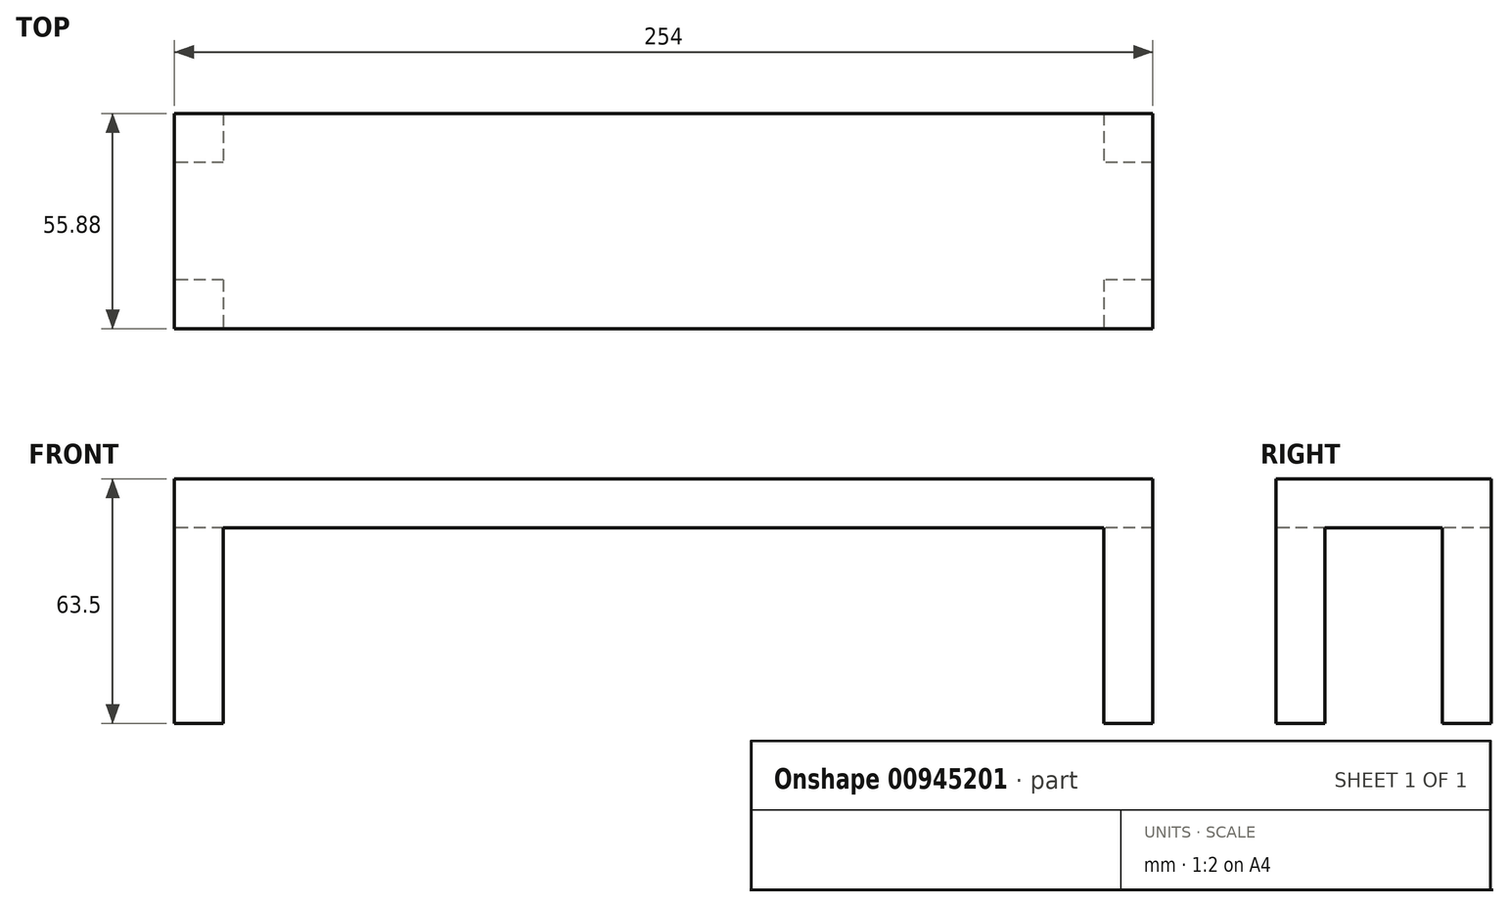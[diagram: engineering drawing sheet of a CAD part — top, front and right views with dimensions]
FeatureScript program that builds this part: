
annotation { "Feature Type Name" : "Feature", "Feature Type Description" : "" }
export const myFeature = defineFeature(function(context is Context, id is Id, definition is map)
    precondition{}
    {
        {
            var Q0;
            Q0=qCreatedBy(makeId("Top.planeOp"),FACE);
            var sketch = newSketch(context, id + "F0", { "sketchPlane" : qUnion([Q0])});
            skLineSegment(sketch, "E0.bottom", {"start": v(-235.66, 41.04) * mm, "end": v(18.34, 41.04) * mm});
            skLineSegment(sketch, "E0.top", {"start": v(-235.66, -14.84) * mm, "end": v(18.34, -14.84) * mm});
            skLineSegment(sketch, "E0.left", {"start": v(-235.66, 41.04) * mm, "end": v(-235.66, -14.84) * mm});
            skLineSegment(sketch, "E0.right", {"start": v(18.34, 41.04) * mm, "end": v(18.34, -14.84) * mm});
            skSolve(sketch);
        }
        {
            var Q0;
            Q0=makeQuery(id+"F0.imprint","IMPRINT",FACE,{"disambiguationData":[TD([[makeQuery(id+"F0.imprint","IMPRINT",EDGE,{"derivedFrom":sQuery(id+"F0.wireOp",EDGE,"E0.bottom")}),-1.0]])]});
            extrude(context, id + "F1", {"entities" : qUnion([Q0]), "depth" : 63.5 * mm, "offsetDistance" : 25.4 * mm});
        }
        {
            var Q0;
            Q0=makeQuery(id+"F1.opExtrude","SWEPT_FACE",FACE,{"disambiguationData":[OSD([sQuery(id+"F0.wireOp",EDGE,"E0.top")])]});
            var sketch = newSketch(context, id + "F2", { "sketchPlane" : qUnion([Q0])});
            skLineSegment(sketch, "E1.bottom", {"start": v(-235.66, 0) * mm, "end": v(18.34, 0) * mm});
            skLineSegment(sketch, "E1.top", {"start": v(-235.66, 63.5) * mm, "end": v(18.34, 63.5) * mm});
            skLineSegment(sketch, "E1.left", {"start": v(-235.66, 0) * mm, "end": v(-235.66, 63.5) * mm});
            skLineSegment(sketch, "E1.right", {"start": v(18.34, 0) * mm, "end": v(18.34, 63.5) * mm});
            skLineSegment(sketch, "E2.bottom", {"start": v(-235.66, 0) * mm, "end": v(-222.96, 0) * mm});
            skLineSegment(sketch, "E2.top", {"start": v(-235.66, 63.5) * mm, "end": v(-222.96, 63.5) * mm});
            skLineSegment(sketch, "E2.right", {"start": v(-222.96, 0) * mm, "end": v(-222.96, 63.5) * mm});
            skLineSegment(sketch, "E3.bottom", {"start": v(18.34, 0) * mm, "end": v(5.64, 0) * mm});
            skLineSegment(sketch, "E3.top", {"start": v(18.34, 63.5) * mm, "end": v(5.64, 63.5) * mm});
            skLineSegment(sketch, "E3.right", {"start": v(5.64, 0) * mm, "end": v(5.64, 63.5) * mm});
            skLineSegment(sketch, "E4.bottom", {"start": v(-222.96, 0) * mm, "end": v(5.64, 0) * mm});
            skLineSegment(sketch, "E4.top", {"start": v(-222.96, 50.8) * mm, "end": v(5.64, 50.8) * mm});
            skLineSegment(sketch, "E4.left", {"start": v(-222.96, 0) * mm, "end": v(-222.96, 50.8) * mm});
            skLineSegment(sketch, "E4.right", {"start": v(5.64, 0) * mm, "end": v(5.64, 50.8) * mm});
            skSolve(sketch);
        }
        {
            var Q0;
            {var subQ5=sQuery(id+"F2.wireOp",EDGE,"E4.top");Q0=makeQuery(id+"F2.imprint","IMPRINT",FACE,{"disambiguationData":[TD([[makeQuery(id+"F2.imprint","IMPRINT",EDGE,{"derivedFrom":subQ5}),-1.0]])]});}
            extrude(context, id + "F3", {"entities" : qUnion([Q0]), "operationType" : NewBodyOperationType.REMOVE, "endBound" : BoundingType.THROUGH_ALL, "oppositeDirection" : true, "depth" : 25.4 * mm, "offsetDistance" : 25.4 * mm});
        }
        {
            var Q0;
            Q0=makeQuery(id+"F1.opExtrude","SWEPT_FACE",FACE,{"disambiguationData":[OSD([sQuery(id+"F0.wireOp",EDGE,"E0.left")])]});
            var sketch = newSketch(context, id + "F4", { "sketchPlane" : qUnion([Q0])});
            skLineSegment(sketch, "E5.bottom", {"start": v(-41.04, 63.5) * mm, "end": v(14.84, 63.5) * mm});
            skLineSegment(sketch, "E5.top", {"start": v(-41.04, 50.8) * mm, "end": v(14.84, 50.8) * mm});
            skLineSegment(sketch, "E5.left", {"start": v(-41.04, 63.5) * mm, "end": v(-41.04, 50.8) * mm});
            skLineSegment(sketch, "E5.right", {"start": v(14.84, 63.5) * mm, "end": v(14.84, 50.8) * mm});
            skLineSegment(sketch, "E6.bottom", {"start": v(-41.04, 0) * mm, "end": v(-28.34, 0) * mm});
            skLineSegment(sketch, "E6.top", {"start": v(-41.04, 63.5) * mm, "end": v(-28.34, 63.5) * mm});
            skLineSegment(sketch, "E6.left", {"start": v(-41.04, 0) * mm, "end": v(-41.04, 63.5) * mm});
            skLineSegment(sketch, "E6.right", {"start": v(-28.34, 0) * mm, "end": v(-28.34, 63.5) * mm});
            skLineSegment(sketch, "E7.bottom", {"start": v(14.84, 0) * mm, "end": v(2.14, 0) * mm});
            skLineSegment(sketch, "E7.top", {"start": v(14.84, 63.5) * mm, "end": v(2.14, 63.5) * mm});
            skLineSegment(sketch, "E7.left", {"start": v(14.84, 0) * mm, "end": v(14.84, 63.5) * mm});
            skLineSegment(sketch, "E7.right", {"start": v(2.14, 0) * mm, "end": v(2.14, 63.5) * mm});
            skLineSegment(sketch, "E8.bottom", {"start": v(-28.34, 0) * mm, "end": v(2.14, 0) * mm});
            skLineSegment(sketch, "E8.top", {"start": v(-28.34, 50.8) * mm, "end": v(2.14, 50.8) * mm});
            skLineSegment(sketch, "E8.left", {"start": v(-28.34, 0) * mm, "end": v(-28.34, 50.8) * mm});
            skLineSegment(sketch, "E8.right", {"start": v(2.14, 0) * mm, "end": v(2.14, 50.8) * mm});
            skSolve(sketch);
        }
        {
            var Q0;
            {var subQ5=sQuery(id+"F4.wireOp",EDGE,"E8.bottom");Q0=makeQuery(id+"F4.imprint","IMPRINT",FACE,{"disambiguationData":[TD([[makeQuery(id+"F4.imprint","IMPRINT",EDGE,{"derivedFrom":subQ5}),1.0]])]});}
            extrude(context, id + "F5", {"entities" : qUnion([Q0]), "operationType" : NewBodyOperationType.REMOVE, "endBound" : BoundingType.THROUGH_ALL, "oppositeDirection" : true, "depth" : 25.4 * mm, "offsetDistance" : 25.4 * mm});
        }
    });
